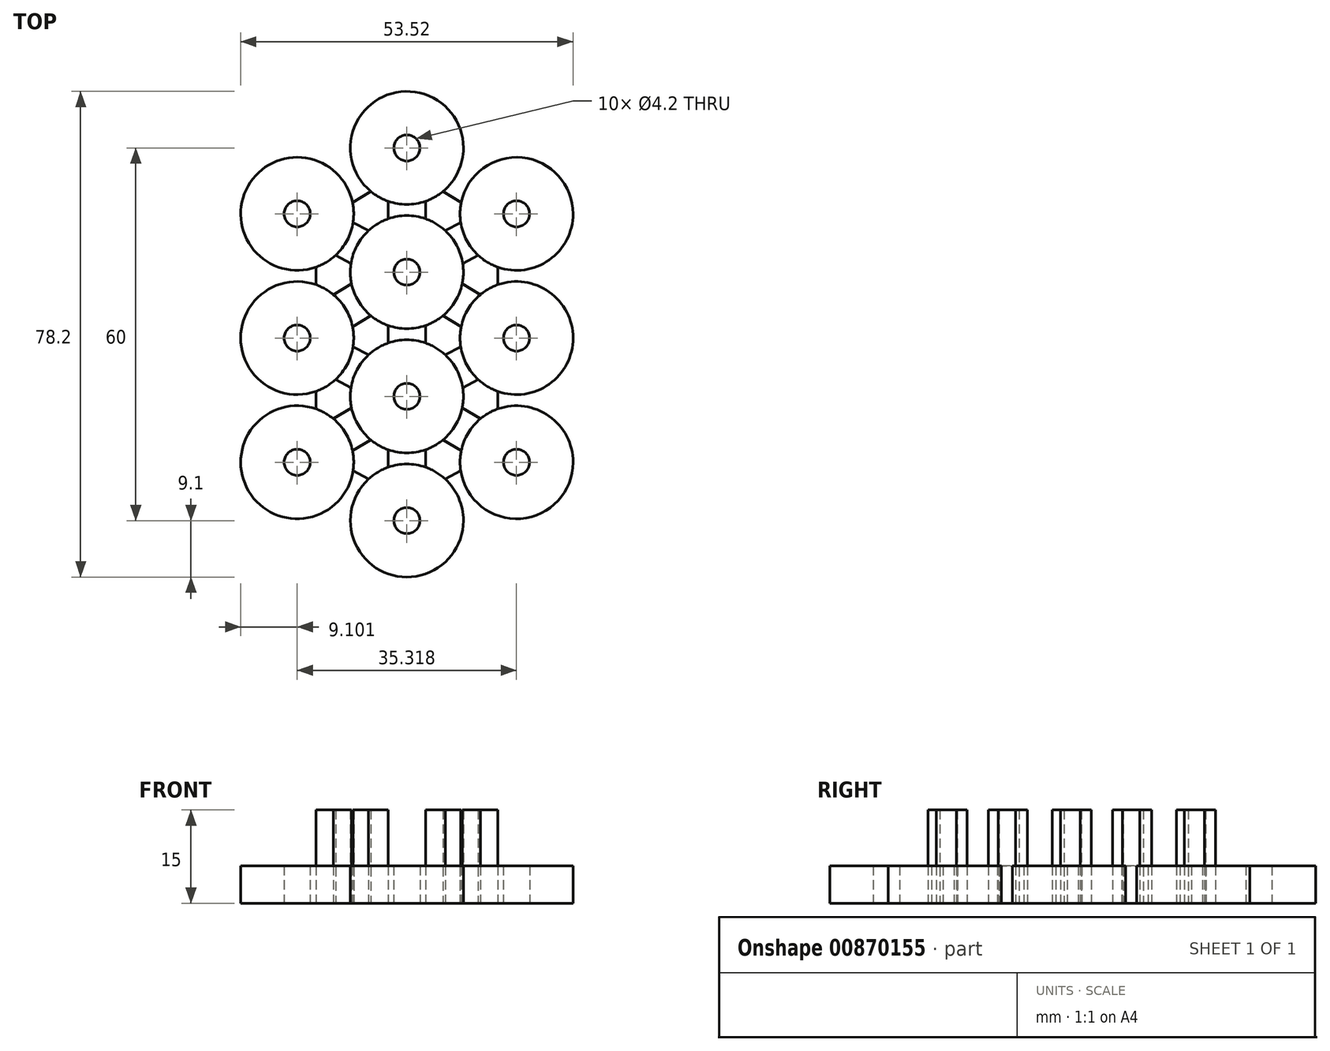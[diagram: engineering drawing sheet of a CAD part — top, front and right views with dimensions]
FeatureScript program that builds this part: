
annotation { "Feature Type Name" : "Feature", "Feature Type Description" : "" }
export const myFeature = defineFeature(function(context is Context, id is Id, definition is map)
    precondition{}
    {
        {
            var Q0;
            Q0=qCreatedBy(makeId("Top.planeOp"),FACE);
            var sketch = newSketch(context, id + "F0", { "sketchPlane" : qUnion([Q0])});
            skLineSegment(sketch, "E0", {"start": v(0, 0) * mm, "end": v(0, 20) * mm, "construction": true});
            skLineSegment(sketch, "E1", {"start": v(0, 20) * mm, "end": v(0, 40) * mm, "construction": true});
            skLineSegment(sketch, "E2", {"start": v(0, 0) * mm, "end": v(-17.66, 9.39) * mm, "construction": true});
            skLineSegment(sketch, "E3", {"start": v(0, 0) * mm, "end": v(17.66, 9.39) * mm, "construction": true});
            skLineSegment(sketch, "E4", {"start": v(0, 20) * mm, "end": v(-17.66, 29.39) * mm, "construction": true});
            skLineSegment(sketch, "E5", {"start": v(0, 20) * mm, "end": v(17.66, 29.39) * mm, "construction": true});
            skLineSegment(sketch, "E6", {"start": v(0, 40) * mm, "end": v(-17.66, 49.39) * mm, "construction": true});
            skLineSegment(sketch, "E7", {"start": v(0, 40) * mm, "end": v(17.66, 49.39) * mm, "construction": true});
            skCircle(sketch, "E8", {"center": v(-17.66, 49.39) * mm, "radius": 9.1 * mm});
            skCircle(sketch, "E9", {"center": v(-17.66, 29.39) * mm, "radius": 9.1 * mm});
            skCircle(sketch, "E10", {"center": v(-17.66, 9.39) * mm, "radius": 9.1 * mm});
            skCircle(sketch, "E11", {"center": v(17.66, 49.39) * mm, "radius": 9.1 * mm});
            skCircle(sketch, "E12", {"center": v(17.66, 29.39) * mm, "radius": 9.1 * mm});
            skCircle(sketch, "E13", {"center": v(17.66, 9.39) * mm, "radius": 9.1 * mm});
            skCircle(sketch, "E14", {"center": v(0, 40) * mm, "radius": 9.1 * mm});
            skCircle(sketch, "E15", {"center": v(0, 20) * mm, "radius": 9.1 * mm});
            skCircle(sketch, "E16", {"center": v(0, 0) * mm, "radius": 9.1 * mm});
            skLineSegment(sketch, "E17", {"start": v(0, 40) * mm, "end": v(0, 60) * mm, "construction": true});
            skCircle(sketch, "E18", {"center": v(0, 60) * mm, "radius": 9.1 * mm});
            skLineSegment(sketch, "E19", {"start": v(-28.76, 60) * mm, "end": v(-28.76, 0) * mm});
            skLineSegment(sketch, "E20", {"start": v(28.76, 60) * mm, "end": v(28.76, 0) * mm});
            skLineSegment(sketch, "E21", {"start": v(0, 0) * mm, "end": v(0, -9.1) * mm, "construction": true});
            skLineSegment(sketch, "E22", {"start": v(-17.66, 49.39) * mm, "end": v(-17.66, 9.39) * mm, "construction": true});
            skLineSegment(sketch, "E23", {"start": v(17.66, 49.39) * mm, "end": v(17.66, 9.39) * mm, "construction": true});
            skLineSegment(sketch, "E24", {"start": v(-17.66, 71.1) * mm, "end": v(17.66, 71.1) * mm});
            skLineSegment(sketch, "E25", {"start": v(17.66, 71.1) * mm, "end": v(28.76, 60) * mm});
            skLineSegment(sketch, "E26", {"start": v(-17.66, 71.1) * mm, "end": v(-28.76, 60) * mm});
            skLineSegment(sketch, "E27", {"start": v(-17.66, -11.1) * mm, "end": v(17.66, -11.1) * mm});
            skLineSegment(sketch, "E28", {"start": v(17.66, -11.1) * mm, "end": v(28.76, 0) * mm});
            skLineSegment(sketch, "E29", {"start": v(-17.66, -11.1) * mm, "end": v(-28.76, 0) * mm});
            skLineSegment(sketch, "E30", {"start": v(-8.66, 48) * mm, "end": v(-6.18, 46.68) * mm});
            skLineSegment(sketch, "E31", {"start": v(-11.48, 42.7) * mm, "end": v(-9, 41.38) * mm});
            skLineSegment(sketch, "E32", {"start": v(-3, 51.4) * mm, "end": v(-3, 48.6) * mm});
            skLineSegment(sketch, "E33", {"start": v(3, 51.4) * mm, "end": v(3, 48.6) * mm});
            skLineSegment(sketch, "E34", {"start": v(6.18, 46.68) * mm, "end": v(8.66, 48) * mm});
            skLineSegment(sketch, "E35", {"start": v(9, 41.38) * mm, "end": v(11.48, 42.7) * mm});
            skLineSegment(sketch, "E36", {"start": v(14.66, 40.8) * mm, "end": v(14.66, 37.98) * mm});
            skLineSegment(sketch, "E37", {"start": v(20.66, 40.8) * mm, "end": v(20.66, 37.98) * mm});
            skLineSegment(sketch, "E38", {"start": v(14.66, 20.8) * mm, "end": v(14.66, 17.98) * mm});
            skLineSegment(sketch, "E39", {"start": v(20.66, 20.8) * mm, "end": v(20.66, 17.98) * mm});
            skLineSegment(sketch, "E40", {"start": v(6.18, 26.68) * mm, "end": v(8.66, 28) * mm});
            skLineSegment(sketch, "E41", {"start": v(11.48, 22.7) * mm, "end": v(9, 21.38) * mm});
            skLineSegment(sketch, "E42", {"start": v(-3, 31.4) * mm, "end": v(-3, 28.6) * mm});
            skLineSegment(sketch, "E43", {"start": v(3, 31.4) * mm, "end": v(3, 28.6) * mm});
            skLineSegment(sketch, "E44", {"start": v(-3, 11.4) * mm, "end": v(-3, 8.6) * mm});
            skLineSegment(sketch, "E45", {"start": v(3, 11.4) * mm, "end": v(3, 8.6) * mm});
            skLineSegment(sketch, "E46", {"start": v(-8.66, 8) * mm, "end": v(-6.18, 6.68) * mm});
            skLineSegment(sketch, "E47", {"start": v(-11.48, 2.7) * mm, "end": v(-9, 1.38) * mm});
            skLineSegment(sketch, "E48", {"start": v(-8.66, 28) * mm, "end": v(-6.18, 26.68) * mm});
            skLineSegment(sketch, "E49", {"start": v(-11.48, 22.7) * mm, "end": v(-9, 21.38) * mm});
            skLineSegment(sketch, "E50", {"start": v(-20.66, 20.8) * mm, "end": v(-20.66, 17.98) * mm});
            skLineSegment(sketch, "E51", {"start": v(-14.66, 20.8) * mm, "end": v(-14.66, 17.98) * mm});
            skLineSegment(sketch, "E52", {"start": v(0, 20) * mm, "end": v(-17.66, 9.39) * mm, "construction": true});
            skLineSegment(sketch, "E53", {"start": v(0, 20) * mm, "end": v(17.66, 9.39) * mm, "construction": true});
            skLineSegment(sketch, "E54", {"start": v(0, 40) * mm, "end": v(-17.66, 29.39) * mm, "construction": true});
            skLineSegment(sketch, "E55", {"start": v(0, 40) * mm, "end": v(17.66, 29.39) * mm, "construction": true});
            skLineSegment(sketch, "E56", {"start": v(-5.82, 13) * mm, "end": v(-8.75, 11.24) * mm});
            skLineSegment(sketch, "E57", {"start": v(-8.9, 18.15) * mm, "end": v(-11.84, 16.39) * mm});
            skLineSegment(sketch, "E58", {"start": v(8.66, 8) * mm, "end": v(6.18, 6.68) * mm});
            skLineSegment(sketch, "E59", {"start": v(11.48, 2.7) * mm, "end": v(9, 1.38) * mm});
            skLineSegment(sketch, "E60", {"start": v(-8.9, 38.15) * mm, "end": v(-11.84, 36.39) * mm});
            skLineSegment(sketch, "E61", {"start": v(-5.82, 33) * mm, "end": v(-8.75, 31.24) * mm});
            skLineSegment(sketch, "E62", {"start": v(5.82, 13) * mm, "end": v(8.75, 11.24) * mm});
            skLineSegment(sketch, "E63", {"start": v(8.9, 18.15) * mm, "end": v(11.84, 16.39) * mm});
            skLineSegment(sketch, "E64", {"start": v(8.9, 38.15) * mm, "end": v(11.84, 36.39) * mm});
            skLineSegment(sketch, "E65", {"start": v(5.82, 33) * mm, "end": v(8.75, 31.24) * mm});
            skLineSegment(sketch, "E66", {"start": v(-14.66, 40.8) * mm, "end": v(-14.66, 37.98) * mm});
            skLineSegment(sketch, "E67", {"start": v(-20.66, 40.8) * mm, "end": v(-20.66, 37.98) * mm});
            skLineSegment(sketch, "E68", {"start": v(0, 60) * mm, "end": v(17.66, 49.39) * mm, "construction": true});
            skLineSegment(sketch, "E69", {"start": v(0, 60) * mm, "end": v(-17.66, 49.39) * mm, "construction": true});
            skLineSegment(sketch, "E70", {"start": v(-5.82, 53) * mm, "end": v(-8.75, 51.24) * mm});
            skLineSegment(sketch, "E71", {"start": v(-8.9, 58.15) * mm, "end": v(-11.84, 56.39) * mm});
            skLineSegment(sketch, "E72", {"start": v(8.9, 58.15) * mm, "end": v(11.84, 56.39) * mm});
            skLineSegment(sketch, "E73", {"start": v(5.82, 53) * mm, "end": v(8.75, 51.24) * mm});
            skCircle(sketch, "E74", {"center": v(-17.66, 49.39) * mm, "radius": 2.1 * mm});
            skCircle(sketch, "E75", {"center": v(0, 60) * mm, "radius": 2.1 * mm});
            skCircle(sketch, "E76", {"center": v(17.66, 29.39) * mm, "radius": 2.1 * mm});
            skCircle(sketch, "E77", {"center": v(0, 20) * mm, "radius": 2.1 * mm});
            skCircle(sketch, "E78", {"center": v(-17.66, 9.39) * mm, "radius": 2.1 * mm});
            skCircle(sketch, "E79", {"center": v(0, 40) * mm, "radius": 2.1 * mm});
            skCircle(sketch, "E80", {"center": v(17.66, 49.39) * mm, "radius": 2.1 * mm});
            skCircle(sketch, "E81", {"center": v(-17.66, 29.39) * mm, "radius": 2.1 * mm});
            skCircle(sketch, "E82", {"center": v(17.66, 9.39) * mm, "radius": 2.1 * mm});
            skCircle(sketch, "E83", {"center": v(0, 0) * mm, "radius": 2.1 * mm});
            skSolve(sketch);
        }
        {
            var Q0;
            Q0=makeQuery(id+"F0.imprint","IMPRINT",FACE,{"disambiguationData":[TD([[makeQuery(id+"F0.imprint","IMPRINT",EDGE,{"derivedFrom":sQuery(id+"F0.wireOp",EDGE,"E19")}),1.0]])]});
            var Q1;
            {var subQ0=sQuery(id+"F0.wireOp",EDGE,"E30");Q1=makeQuery(id+"F0.imprint","IMPRINT",FACE,{"disambiguationData":[TD([[makeQuery(id+"F0.imprint","IMPRINT",EDGE,{"derivedFrom":subQ0}),1.0]])]});}
            var Q2;
            {var subQ0=sQuery(id+"F0.wireOp",EDGE,"E33");Q2=makeQuery(id+"F0.imprint","IMPRINT",FACE,{"disambiguationData":[TD([[makeQuery(id+"F0.imprint","IMPRINT",EDGE,{"derivedFrom":subQ0}),1.0]])]});}
            var Q3;
            {var subQ0=sQuery(id+"F0.wireOp",EDGE,"E35");Q3=makeQuery(id+"F0.imprint","IMPRINT",FACE,{"disambiguationData":[TD([[makeQuery(id+"F0.imprint","IMPRINT",EDGE,{"derivedFrom":subQ0}),-1.0]])]});}
            var Q4;
            {var subQ0=sQuery(id+"F0.wireOp",EDGE,"E31");Q4=makeQuery(id+"F0.imprint","IMPRINT",FACE,{"disambiguationData":[TD([[makeQuery(id+"F0.imprint","IMPRINT",EDGE,{"derivedFrom":subQ0}),-1.0]])]});}
            var Q5;
            {var subQ0=sQuery(id+"F0.wireOp",EDGE,"E42");Q5=makeQuery(id+"F0.imprint","IMPRINT",FACE,{"disambiguationData":[TD([[makeQuery(id+"F0.imprint","IMPRINT",EDGE,{"derivedFrom":subQ0}),-1.0]])]});}
            var Q6;
            {var subQ0=sQuery(id+"F0.wireOp",EDGE,"E40");Q6=makeQuery(id+"F0.imprint","IMPRINT",FACE,{"disambiguationData":[TD([[makeQuery(id+"F0.imprint","IMPRINT",EDGE,{"derivedFrom":subQ0}),1.0]])]});}
            var Q7;
            {var subQ0=sQuery(id+"F0.wireOp",EDGE,"E38");Q7=makeQuery(id+"F0.imprint","IMPRINT",FACE,{"disambiguationData":[TD([[makeQuery(id+"F0.imprint","IMPRINT",EDGE,{"derivedFrom":subQ0}),-1.0]])]});}
            var Q8;
            {var subQ0=sQuery(id+"F0.wireOp",EDGE,"E45");Q8=makeQuery(id+"F0.imprint","IMPRINT",FACE,{"disambiguationData":[TD([[makeQuery(id+"F0.imprint","IMPRINT",EDGE,{"derivedFrom":subQ0}),1.0]])]});}
            var Q9;
            {var subQ0=sQuery(id+"F0.wireOp",EDGE,"E49");Q9=makeQuery(id+"F0.imprint","IMPRINT",FACE,{"disambiguationData":[TD([[makeQuery(id+"F0.imprint","IMPRINT",EDGE,{"derivedFrom":subQ0}),-1.0]])]});}
            var Q10;
            {var subQ0=sQuery(id+"F0.wireOp",EDGE,"E44");Q10=makeQuery(id+"F0.imprint","IMPRINT",FACE,{"disambiguationData":[TD([[makeQuery(id+"F0.imprint","IMPRINT",EDGE,{"derivedFrom":subQ0}),-1.0]])]});}
            extrude(context, id + "F1", {"entities" : qUnion([Q0, Q1, Q2, Q3, Q4, Q5, Q6, Q7, Q8, Q9, Q10]), "depth" : 15 * mm, "offsetDistance" : 25 * mm});
        }
        {
            var Q0;
            {var subQ0=sQuery(id+"F0.wireOp",EDGE,"E18");var subQ4=makeQuery(id+"F0.imprint","INTERSECT",VERTEX,{"derivedFrom":[subQ0,sQuery(id+"F0.wireOp",EDGE,"E70")]});Q0=makeQuery(id+"F0.imprint","IMPRINT",FACE,{"disambiguationData":[TD([[makeQuery(id+"F0.imprint","IMPRINT",EDGE,{"disambiguationData":[TD([[subQ4,1.0]])],"derivedFrom":subQ0}),1.0]])]});}
            var Q1;
            {var subQ0=sQuery(id+"F0.wireOp",EDGE,"E11");var subQ5=makeQuery(id+"F0.imprint","INTERSECT",VERTEX,{"derivedFrom":[subQ0,sQuery(id+"F0.wireOp",EDGE,"E72")]});Q1=makeQuery(id+"F0.imprint","IMPRINT",FACE,{"disambiguationData":[TD([[makeQuery(id+"F0.imprint","IMPRINT",EDGE,{"disambiguationData":[TD([[subQ5,-1.0]])],"derivedFrom":subQ0}),1.0]])]});}
            var Q2;
            {var subQ0=sQuery(id+"F0.wireOp",EDGE,"E8");var subQ5=makeQuery(id+"F0.imprint","INTERSECT",VERTEX,{"derivedFrom":[subQ0,sQuery(id+"F0.wireOp",EDGE,"E70")]});Q2=makeQuery(id+"F0.imprint","IMPRINT",FACE,{"disambiguationData":[TD([[makeQuery(id+"F0.imprint","IMPRINT",EDGE,{"disambiguationData":[TD([[subQ5,-1.0]])],"derivedFrom":subQ0}),1.0]])]});}
            var Q3;
            {var subQ0=sQuery(id+"F0.wireOp",EDGE,"E9");var subQ4=makeQuery(id+"F0.imprint","INTERSECT",VERTEX,{"derivedFrom":[subQ0,sQuery(id+"F0.wireOp",EDGE,"E60")]});Q3=makeQuery(id+"F0.imprint","IMPRINT",FACE,{"disambiguationData":[TD([[makeQuery(id+"F0.imprint","IMPRINT",EDGE,{"disambiguationData":[TD([[subQ4,1.0]])],"derivedFrom":subQ0}),1.0]])]});}
            var Q4;
            {var subQ0=sQuery(id+"F0.wireOp",EDGE,"E12");var subQ4=makeQuery(id+"F0.imprint","INTERSECT",VERTEX,{"derivedFrom":[subQ0,sQuery(id+"F0.wireOp",EDGE,"E36")]});Q4=makeQuery(id+"F0.imprint","IMPRINT",FACE,{"disambiguationData":[TD([[makeQuery(id+"F0.imprint","IMPRINT",EDGE,{"disambiguationData":[TD([[subQ4,1.0]])],"derivedFrom":subQ0}),1.0]])]});}
            var Q5;
            {var subQ0=sQuery(id+"F0.wireOp",EDGE,"E14");var subQ8=makeQuery(id+"F0.imprint","INTERSECT",VERTEX,{"derivedFrom":[subQ0,sQuery(id+"F0.wireOp",EDGE,"E34")]});Q5=makeQuery(id+"F0.imprint","IMPRINT",FACE,{"disambiguationData":[TD([[makeQuery(id+"F0.imprint","IMPRINT",EDGE,{"disambiguationData":[TD([[subQ8,1.0]])],"derivedFrom":subQ0}),1.0]])]});}
            var Q6;
            {var subQ0=sQuery(id+"F0.wireOp",EDGE,"E15");var subQ8=makeQuery(id+"F0.imprint","INTERSECT",VERTEX,{"derivedFrom":[subQ0,sQuery(id+"F0.wireOp",EDGE,"E40")]});Q6=makeQuery(id+"F0.imprint","IMPRINT",FACE,{"disambiguationData":[TD([[makeQuery(id+"F0.imprint","IMPRINT",EDGE,{"disambiguationData":[TD([[subQ8,1.0]])],"derivedFrom":subQ0}),1.0]])]});}
            var Q7;
            {var subQ0=sQuery(id+"F0.wireOp",EDGE,"E13");var subQ4=makeQuery(id+"F0.imprint","INTERSECT",VERTEX,{"derivedFrom":[subQ0,sQuery(id+"F0.wireOp",EDGE,"E38")]});Q7=makeQuery(id+"F0.imprint","IMPRINT",FACE,{"disambiguationData":[TD([[makeQuery(id+"F0.imprint","IMPRINT",EDGE,{"disambiguationData":[TD([[subQ4,1.0]])],"derivedFrom":subQ0}),1.0]])]});}
            var Q8;
            {var subQ0=sQuery(id+"F0.wireOp",EDGE,"E16");var subQ4=makeQuery(id+"F0.imprint","INTERSECT",VERTEX,{"derivedFrom":[subQ0,sQuery(id+"F0.wireOp",EDGE,"E58")]});Q8=makeQuery(id+"F0.imprint","IMPRINT",FACE,{"disambiguationData":[TD([[makeQuery(id+"F0.imprint","IMPRINT",EDGE,{"disambiguationData":[TD([[subQ4,1.0]])],"derivedFrom":subQ0}),1.0]])]});}
            var Q9;
            {var subQ0=sQuery(id+"F0.wireOp",EDGE,"E10");var subQ5=makeQuery(id+"F0.imprint","INTERSECT",VERTEX,{"derivedFrom":[subQ0,sQuery(id+"F0.wireOp",EDGE,"E56")]});Q9=makeQuery(id+"F0.imprint","IMPRINT",FACE,{"disambiguationData":[TD([[makeQuery(id+"F0.imprint","IMPRINT",EDGE,{"disambiguationData":[TD([[subQ5,-1.0]])],"derivedFrom":subQ0}),1.0]])]});}
            extrude(context, id + "F2", {"entities" : qUnion([Q0, Q1, Q2, Q3, Q4, Q5, Q6, Q7, Q8, Q9]), "depth" : 6 * mm, "offsetDistance" : 25 * mm});
        }
    });
